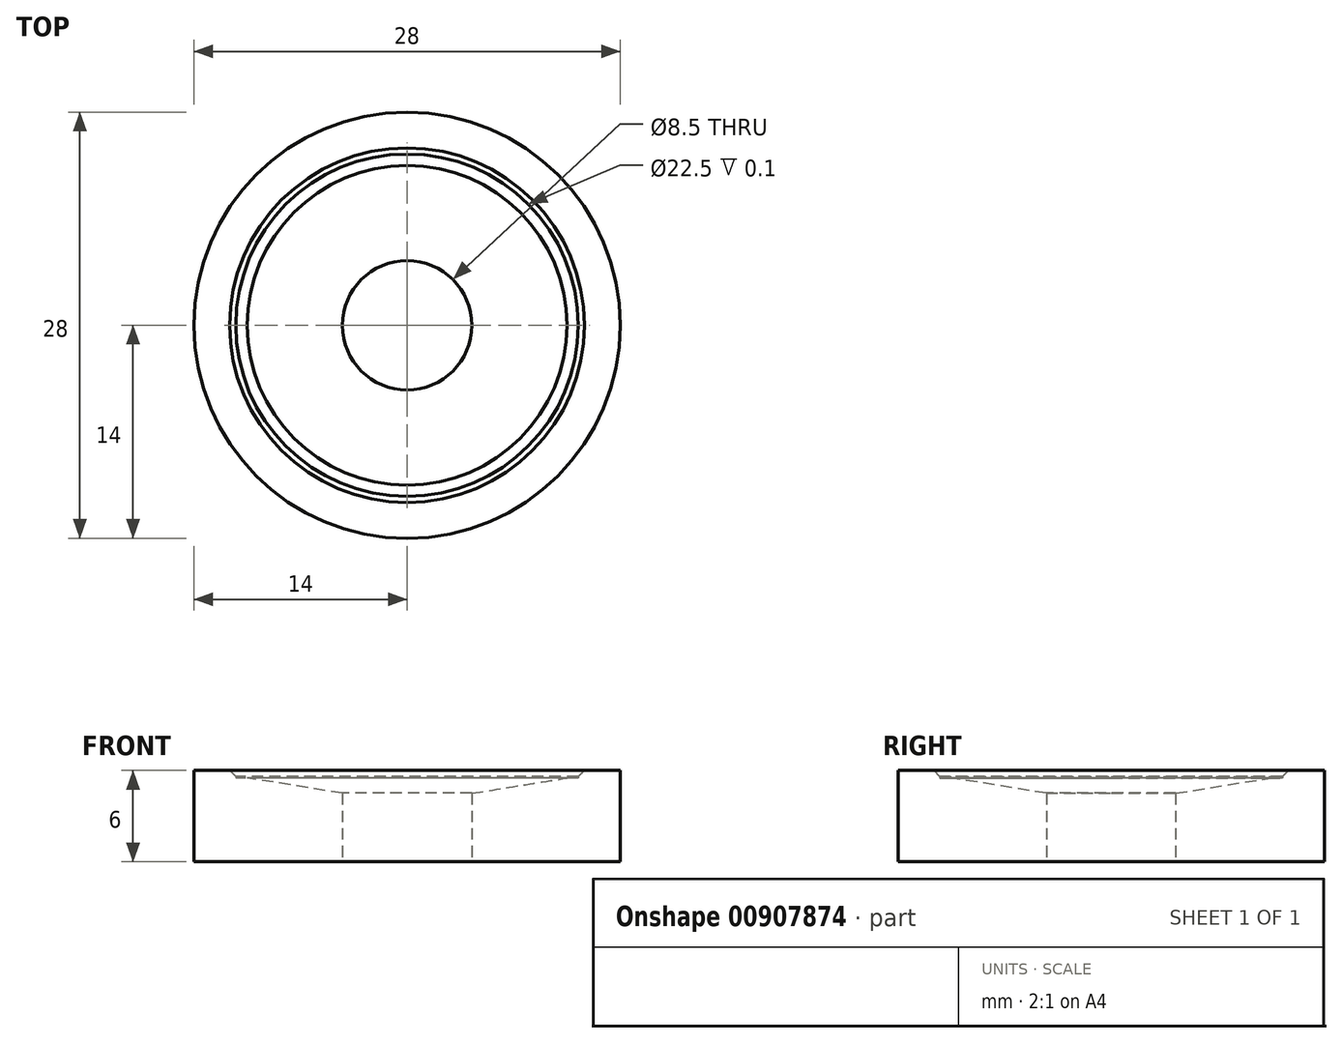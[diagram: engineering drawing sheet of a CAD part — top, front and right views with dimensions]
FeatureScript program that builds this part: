
annotation { "Feature Type Name" : "Feature", "Feature Type Description" : "" }
export const myFeature = defineFeature(function(context is Context, id is Id, definition is map)
    precondition{}
    {
        {
            var Q0;
            Q0=qCreatedBy(makeId("Top.planeOp"),FACE);
            var sketch = newSketch(context, id + "F0", { "sketchPlane" : qUnion([Q0])});
            skCircle(sketch, "E0", {"center": v(0, 0) * mm, "radius": 14 * mm});
            skCircle(sketch, "E1", {"center": v(0, 0) * mm, "radius": 4.25 * mm});
            skCircle(sketch, "E2", {"center": v(0, 0) * mm, "radius": 11.25 * mm});
            skSolve(sketch);
        }
        {
            var Q0;
            Q0=makeQuery(id+"F0.imprint","IMPRINT",FACE,{"disambiguationData":[TD([[makeQuery(id+"F0.imprint","IMPRINT",EDGE,{"derivedFrom":sQuery(id+"F0.wireOp",EDGE,"E1")}),-1.0]])]});
            extrude(context, id + "F1", {"entities" : qUnion([Q0]), "depth" : 5.5 * mm, "offsetDistance" : 25 * mm});
        }
        {
            var Q0;
            Q0=makeQuery(id+"F1.opExtrude","CAP_EDGE",EDGE,{"disambiguationData":[OSD([sQuery(id+"F0.wireOp",EDGE,"E1")])],"isStart":false});
            chamfer(context, id + "F2", {"entities" : qUnion([Q0]), "chamferType" : ChamferType.TWO_OFFSETS, "width1" : 1 * mm, "oppositeDirection" : false, "width2" : 6.25 * mm, "tangentPropagation" : true});
        }
        {
            var Q0;
            Q0=makeQuery(id+"F0.imprint","IMPRINT",FACE,{"disambiguationData":[TD([[makeQuery(id+"F0.imprint","IMPRINT",EDGE,{"derivedFrom":sQuery(id+"F0.wireOp",EDGE,"E0")}),1.0]])]});
            extrude(context, id + "F3", {"entities" : qUnion([Q0]), "operationType" : NewBodyOperationType.ADD, "depth" : 6 * mm, "offsetDistance" : 25 * mm});
        }
        {
            var Q0;
            Q0=makeQuery(id+"F3.opExtrude","CAP_EDGE",EDGE,{"disambiguationData":[OSD([sQuery(id+"F0.wireOp",EDGE,"E2")])],"isStart":false});
            chamfer(context, id + "F4", {"entities" : qUnion([Q0]), "width" : .4 * mm, "tangentPropagation" : true});
        }
    });
